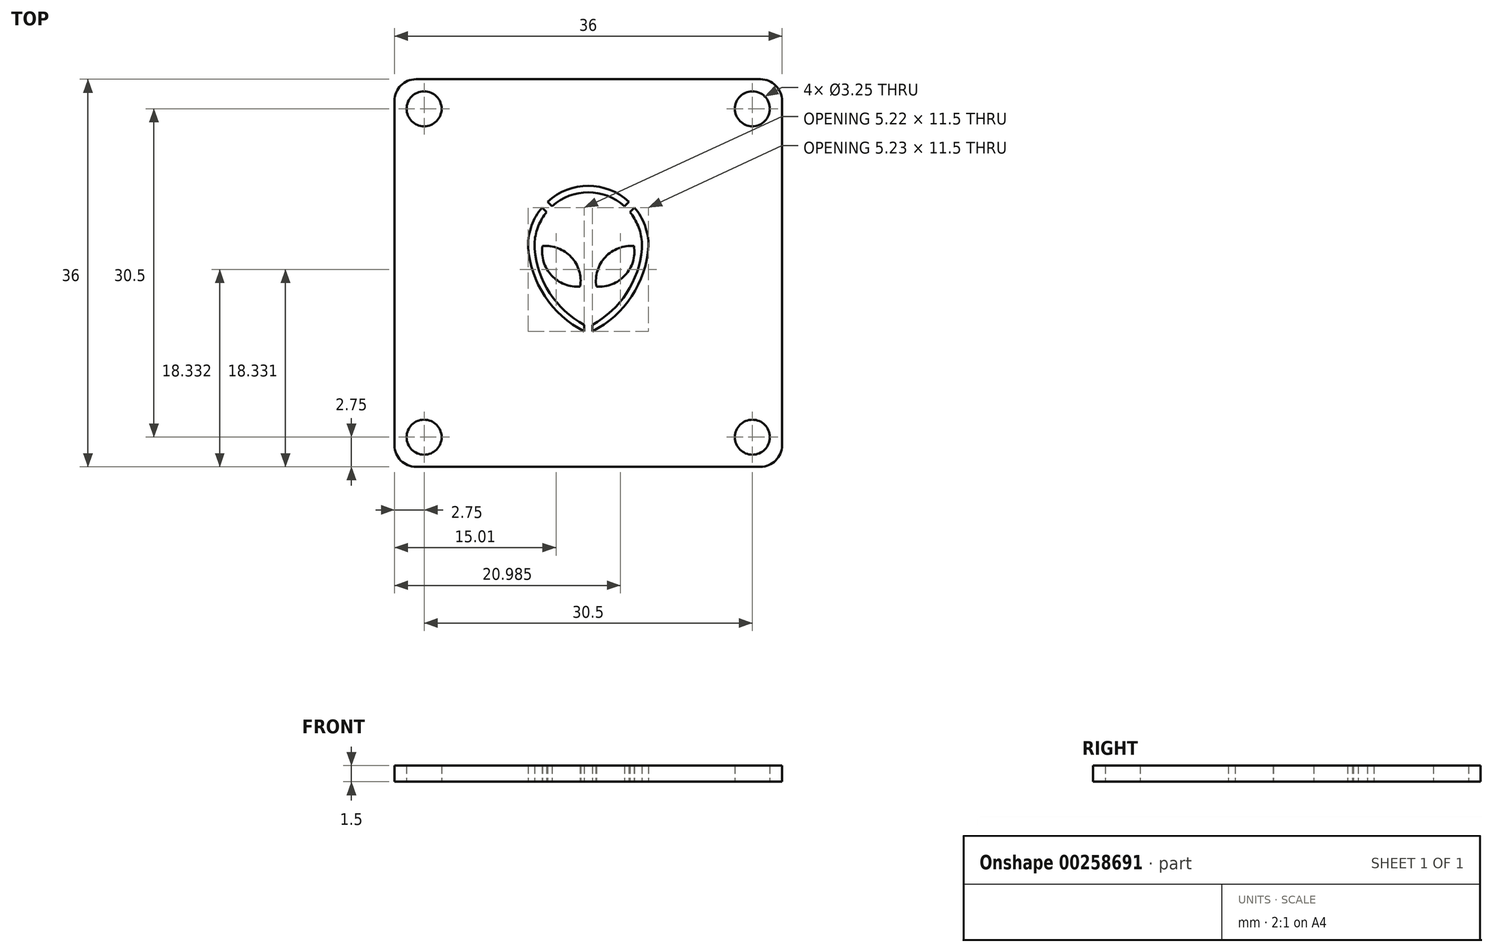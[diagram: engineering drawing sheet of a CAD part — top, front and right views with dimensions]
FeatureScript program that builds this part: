
annotation { "Feature Type Name" : "Feature", "Feature Type Description" : "" }
export const myFeature = defineFeature(function(context is Context, id is Id, definition is map)
    precondition{}
    {
        {
            var Q0;
            Q0=qCreatedBy(makeId("Top.planeOp"),FACE);
            var sketch = newSketch(context, id + "F0", { "sketchPlane" : qUnion([Q0])});
            skLineSegment(sketch, "E0.bottom", {"start": v(0, 0) * mm, "end": v(36, 0) * mm});
            skLineSegment(sketch, "E0.top", {"start": v(0, -36) * mm, "end": v(36, -36) * mm});
            skLineSegment(sketch, "E0.left", {"start": v(0, 0) * mm, "end": v(0, -36) * mm});
            skLineSegment(sketch, "E0.right", {"start": v(36, 0) * mm, "end": v(36, -36) * mm});
            skCircle(sketch, "E1", {"center": v(2.75, -2.75) * mm, "radius": 1.63 * mm});
            skCircle(sketch, "E2", {"center": v(33.25, -2.75) * mm, "radius": 1.63 * mm});
            skCircle(sketch, "E3", {"center": v(33.25, -33.25) * mm, "radius": 1.63 * mm});
            skCircle(sketch, "E4", {"center": v(2.75, -33.25) * mm, "radius": 1.63 * mm});
            skArc(sketch, "E5", {"start": v(23, -15.5) * mm, "mid": v(18, -10.5) * mm, "end": v(13, -15.5) * mm});
            skArc(sketch, "E6", {"start": v(18, -23) * mm, "mid": v(21.53, -19.93) * mm, "end": v(23, -15.5) * mm});
            skArc(sketch, "E7", {"start": v(13, -15.5) * mm, "mid": v(14.47, -19.93) * mm, "end": v(18, -23) * mm});
            skArc(sketch, "E8", {"start": v(22.25, -15.5) * mm, "mid": v(19.59, -16.52) * mm, "end": v(18.75, -19.25) * mm});
            skArc(sketch, "E9", {"start": v(18.75, -19.25) * mm, "mid": v(21.41, -18.23) * mm, "end": v(22.25, -15.5) * mm});
            skArc(sketch, "E10", {"start": v(17.25, -19.25) * mm, "mid": v(16.41, -16.52) * mm, "end": v(13.75, -15.5) * mm});
            skArc(sketch, "E11", {"start": v(13.75, -15.5) * mm, "mid": v(14.59, -18.23) * mm, "end": v(17.25, -19.25) * mm});
            skLineSegment(sketch, "E12", {"start": v(13.52, -15.92) * mm, "end": v(13.71, -15.92) * mm});
            skPoint(sketch, "E13.startSnap0", {"position": v(18, -10.5) * mm});
            skLineSegment(sketch, "E14", {"start": v(18, -23) * mm, "end": v(18, -18) * mm});
            skArc(sketch, "E15", {"start": v(23.6, -15.5) * mm, "mid": v(18, -9.9) * mm, "end": v(12.4, -15.5) * mm});
            skArc(sketch, "E16", {"start": v(18, -23.6) * mm, "mid": v(21.93, -20.33) * mm, "end": v(23.6, -15.5) * mm});
            skArc(sketch, "E17", {"start": v(12.4, -15.5) * mm, "mid": v(14.08, -20.32) * mm, "end": v(18, -23.6) * mm});
            skLineSegment(sketch, "E18", {"start": v(22.1, -12.11) * mm, "end": v(21.87, -12.34) * mm});
            skLineSegment(sketch, "E19", {"start": v(21.87, -12.34) * mm, "end": v(22.3, -11.92) * mm});
            skLineSegment(sketch, "E20", {"start": v(13.9, -12.11) * mm, "end": v(14.13, -12.34) * mm});
            skLineSegment(sketch, "E21", {"start": v(14.13, -12.34) * mm, "end": v(13.7, -11.92) * mm});
            skPoint(sketch, "E22.endSnap0", {"position": v(18, -23.3) * mm});
            skLineSegment(sketch, "E23", {"start": v(18.37, -23.3) * mm, "end": v(18.37, -22.8) * mm});
            skLineSegment(sketch, "E24", {"start": v(18.37, -22.8) * mm, "end": v(18.37, -23.42) * mm});
            skLineSegment(sketch, "E25", {"start": v(17.62, -23.3) * mm, "end": v(17.62, -22.8) * mm});
            skLineSegment(sketch, "E26", {"start": v(17.62, -23.3) * mm, "end": v(17.62, -23.42) * mm});
            skLineSegment(sketch, "E27", {"start": v(21.57, -11.58) * mm, "end": v(21.35, -11.8) * mm});
            skLineSegment(sketch, "E28", {"start": v(21.35, -11.8) * mm, "end": v(21.78, -11.38) * mm});
            skLineSegment(sketch, "E29", {"start": v(14.43, -11.58) * mm, "end": v(14.22, -11.38) * mm});
            skLineSegment(sketch, "E30", {"start": v(14.22, -11.38) * mm, "end": v(14.64, -11.8) * mm});
            skSolve(sketch);
        }
        {
            var Q0;
            Q0=makeQuery(id+"F0.imprint","IMPRINT",FACE,{"disambiguationData":[TD([[makeQuery(id+"F0.imprint","IMPRINT",EDGE,{"derivedFrom":sQuery(id+"F0.wireOp",EDGE,"E8")}),-1.0]])]});
            var Q1;
            {var subQ1=sQuery(id+"F0.wireOp",EDGE,"E20");Q1=makeQuery(id+"F0.imprint","IMPRINT",FACE,{"disambiguationData":[TD([[makeQuery(id+"F0.imprint","IMPRINT",EDGE,{"derivedFrom":subQ1}),1.0]])]});}
            var Q2;
            {var subQ1=sQuery(id+"F0.wireOp",EDGE,"E18");Q2=makeQuery(id+"F0.imprint","IMPRINT",FACE,{"disambiguationData":[TD([[makeQuery(id+"F0.imprint","IMPRINT",EDGE,{"derivedFrom":subQ1}),-1.0]])]});}
            var Q3;
            {var subQ9=sQuery(id+"F0.wireOp",EDGE,"E23");Q3=makeQuery(id+"F0.imprint","IMPRINT",FACE,{"disambiguationData":[TD([[makeQuery(id+"F0.imprint","IMPRINT",EDGE,{"derivedFrom":subQ9}),1.0]])]});}
            var Q4;
            Q4=makeQuery(id+"F0.imprint","IMPRINT",FACE,{"disambiguationData":[TD([[makeQuery(id+"F0.imprint","IMPRINT",EDGE,{"derivedFrom":sQuery(id+"F0.wireOp",EDGE,"E0.bottom")}),-1.0]])]});
            extrude(context, id + "F1", {"entities" : qUnion([Q0, Q1, Q2, Q3, Q4]), "depth" : 1.5 * mm});
        }
        {
            var Q0;
            Q0=makeQuery(id+"F1.opExtrude","SWEPT_EDGE",EDGE,{"disambiguationData":[OSD([sQuery(id+"F0.wireOp",EDGE,"E0.top"),sQuery(id+"F0.wireOp",EDGE,"E0.right")])]});
            var Q1;
            Q1=makeQuery(id+"F1.opExtrude","SWEPT_EDGE",EDGE,{"disambiguationData":[OSD([sQuery(id+"F0.wireOp",EDGE,"E0.top"),sQuery(id+"F0.wireOp",EDGE,"E0.left")])]});
            var Q2;
            Q2=makeQuery(id+"F1.opExtrude","SWEPT_EDGE",EDGE,{"disambiguationData":[OSD([sQuery(id+"F0.wireOp",EDGE,"E0.bottom"),sQuery(id+"F0.wireOp",EDGE,"E0.right")])]});
            var Q3;
            Q3=makeQuery(id+"F1.opExtrude","SWEPT_EDGE",EDGE,{"disambiguationData":[OSD([sQuery(id+"F0.wireOp",EDGE,"E0.bottom"),sQuery(id+"F0.wireOp",EDGE,"E0.left")])]});
            fillet(context, id + "F2", {"entities" : qUnion([Q0, Q1, Q2, Q3]), "radius" : 2 * mm, "tangentPropagation" : true, "allowEdgeOverflow" : false});
        }
        {
            var Q0;
            Q0=makeQuery(id+"F1.opExtrude","SWEPT_EDGE",EDGE,{"disambiguationData":[OSD([sQuery(id+"F0.wireOp",EDGE,"E5"),sQuery(id+"F0.wireOp",EDGE,"E6")])]});
            var Q1;
            Q1=makeQuery(id+"F1.opExtrude","SWEPT_EDGE",EDGE,{"disambiguationData":[OSD([sQuery(id+"F0.wireOp",EDGE,"E5"),sQuery(id+"F0.wireOp",EDGE,"E7")])]});
            fillet(context, id + "F3", {"entities" : qUnion([Q0, Q1]), "radius" : 4 * mm, "tangentPropagation" : true, "allowEdgeOverflow" : false});
        }
    });
